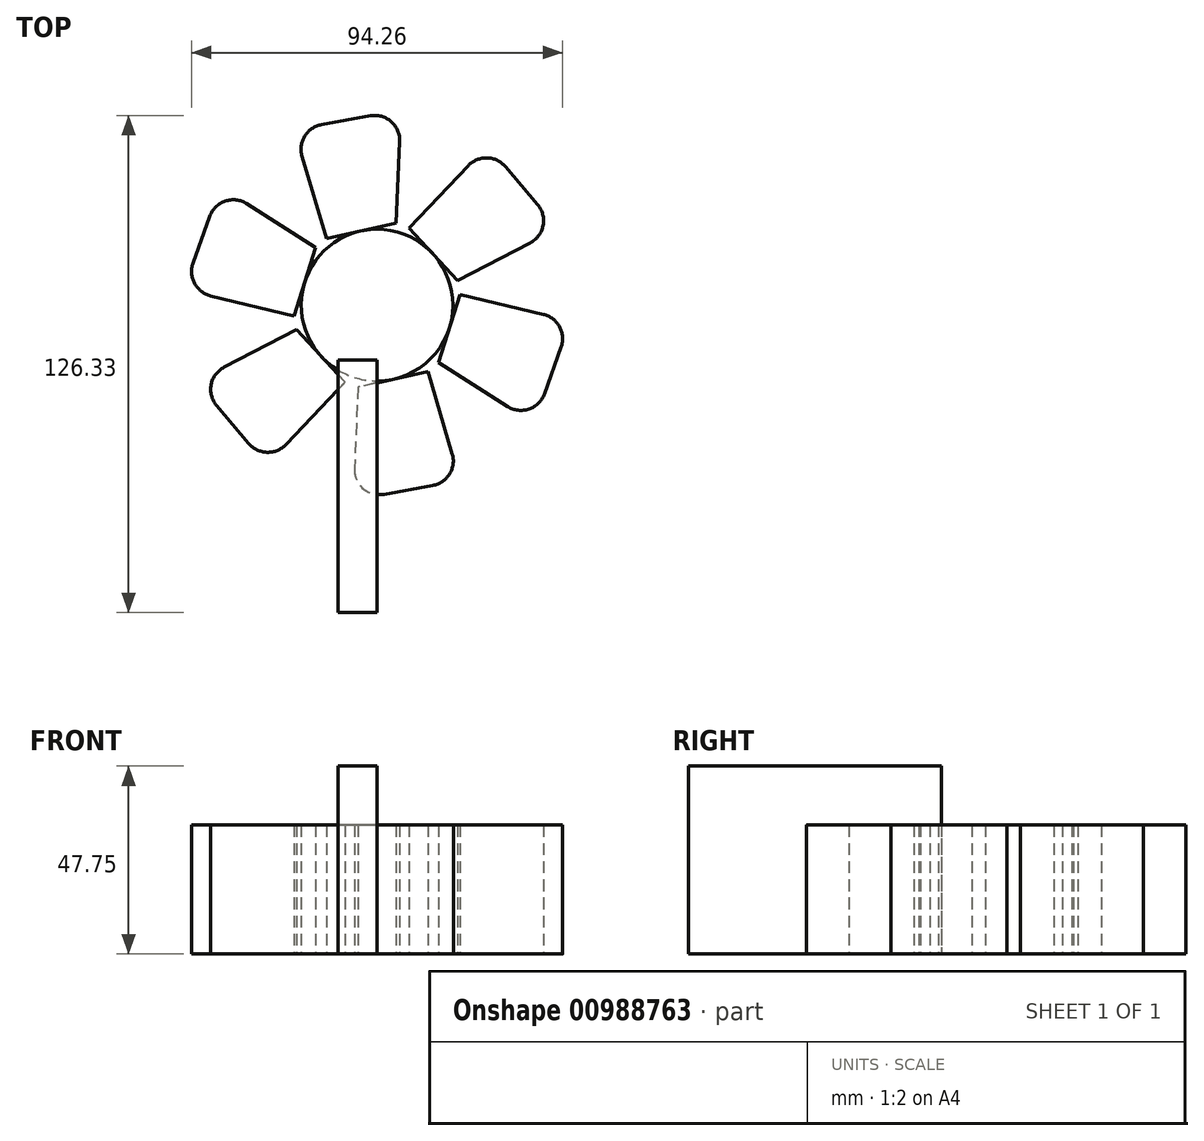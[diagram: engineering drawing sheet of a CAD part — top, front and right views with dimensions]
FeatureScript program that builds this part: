
annotation { "Feature Type Name" : "Feature", "Feature Type Description" : "" }
export const myFeature = defineFeature(function(context is Context, id is Id, definition is map)
    precondition{}
    {
        {
            var Q0;
            Q0=qCreatedBy(makeId("Top.planeOp"),FACE);
            var sketch = newSketch(context, id + "F0", { "sketchPlane" : qUnion([Q0])});
            skCircle(sketch, "E0", {"center": v(0, 0) * mm, "radius": 19.26 * mm});
            skLineSegment(sketch, "E1", {"start": v(8.15, 19.6) * mm, "end": v(20.47, 6.2) * mm});
            skLineSegment(sketch, "E2", {"start": v(20.47, 6.2) * mm, "end": v(38.87, 15.8) * mm});
            skLineSegment(sketch, "E3", {"start": v(40.78, 25.54) * mm, "end": v(32.62, 35.16) * mm});
            skLineSegment(sketch, "E4", {"start": v(23.17, 35.42) * mm, "end": v(8.15, 19.6) * mm});
            skPoint(sketch, "E5.visualSharp", {"position": v(28.04, 40.56) * mm});
            skArc(sketch, "E5.filletArc", {"start": v(32.62, 35.16) * mm, "mid": v(27.95, 37.4) * mm, "end": v(23.17, 35.42) * mm});
            skPoint(sketch, "E6.visualSharp", {"position": v(45.92, 19.47) * mm});
            skArc(sketch, "E6.filletArc", {"start": v(38.87, 15.8) * mm, "mid": v(42.17, 20.2) * mm, "end": v(40.78, 25.54) * mm});
            skArc(sketch, "E7.1.0", {"start": v(-14.14, 45.83) * mm, "mid": v(-18.41, 42.9) * mm, "end": v(-19.1, 37.78) * mm});
            skLineSegment(sketch, "E7.1.1", {"start": v(-1.72, 48.08) * mm, "end": v(-14.14, 45.83) * mm});
            skArc(sketch, "E7.1.2", {"start": v(5.75, 41.56) * mm, "mid": v(3.58, 46.62) * mm, "end": v(-1.72, 48.08) * mm});
            skLineSegment(sketch, "E7.1.3", {"start": v(4.86, 20.83) * mm, "end": v(5.75, 41.56) * mm});
            skLineSegment(sketch, "E7.1.4", {"start": v(-19.1, 37.78) * mm, "end": v(-12.9, 16.85) * mm});
            skLineSegment(sketch, "E7.1.5", {"start": v(-12.9, 16.85) * mm, "end": v(4.86, 20.83) * mm});
            skArc(sketch, "E7.2.0", {"start": v(-46.76, 10.67) * mm, "mid": v(-46.37, 5.5) * mm, "end": v(-42.26, 2.35) * mm});
            skLineSegment(sketch, "E7.2.1", {"start": v(-42.5, 22.55) * mm, "end": v(-46.76, 10.67) * mm});
            skArc(sketch, "E7.2.2", {"start": v(-33.12, 25.76) * mm, "mid": v(-38.58, 26.41) * mm, "end": v(-42.5, 22.55) * mm});
            skLineSegment(sketch, "E7.2.3", {"start": v(-15.6, 14.63) * mm, "end": v(-33.12, 25.76) * mm});
            skLineSegment(sketch, "E7.2.4", {"start": v(-42.26, 2.35) * mm, "end": v(-21.04, -2.74) * mm});
            skLineSegment(sketch, "E7.2.5", {"start": v(-21.04, -2.74) * mm, "end": v(-15.6, 14.63) * mm});
            skArc(sketch, "E7.3.0", {"start": v(-32.62, -35.16) * mm, "mid": v(-27.95, -37.4) * mm, "end": v(-23.17, -35.42) * mm});
            skLineSegment(sketch, "E7.3.1", {"start": v(-40.78, -25.54) * mm, "end": v(-32.62, -35.16) * mm});
            skArc(sketch, "E7.3.2", {"start": v(-38.87, -15.8) * mm, "mid": v(-42.17, -20.2) * mm, "end": v(-40.78, -25.54) * mm});
            skLineSegment(sketch, "E7.3.3", {"start": v(-20.47, -6.2) * mm, "end": v(-38.87, -15.8) * mm});
            skLineSegment(sketch, "E7.3.4", {"start": v(-23.17, -35.42) * mm, "end": v(-8.15, -19.6) * mm});
            skLineSegment(sketch, "E7.3.5", {"start": v(-8.15, -19.6) * mm, "end": v(-20.47, -6.2) * mm});
            skArc(sketch, "E7.4.0", {"start": v(14.14, -45.83) * mm, "mid": v(18.41, -42.9) * mm, "end": v(19.1, -37.78) * mm});
            skLineSegment(sketch, "E7.4.1", {"start": v(1.72, -48.08) * mm, "end": v(14.14, -45.83) * mm});
            skArc(sketch, "E7.4.2", {"start": v(-5.75, -41.56) * mm, "mid": v(-3.58, -46.62) * mm, "end": v(1.72, -48.08) * mm});
            skLineSegment(sketch, "E7.4.3", {"start": v(-4.86, -20.83) * mm, "end": v(-5.75, -41.56) * mm});
            skLineSegment(sketch, "E7.4.4", {"start": v(19.1, -37.78) * mm, "end": v(12.9, -16.85) * mm});
            skLineSegment(sketch, "E7.4.5", {"start": v(12.9, -16.85) * mm, "end": v(-4.86, -20.83) * mm});
            skArc(sketch, "E7.5.0", {"start": v(46.76, -10.67) * mm, "mid": v(46.37, -5.5) * mm, "end": v(42.26, -2.35) * mm});
            skLineSegment(sketch, "E7.5.1", {"start": v(42.5, -22.55) * mm, "end": v(46.76, -10.67) * mm});
            skArc(sketch, "E7.5.2", {"start": v(33.12, -25.76) * mm, "mid": v(38.58, -26.41) * mm, "end": v(42.5, -22.55) * mm});
            skLineSegment(sketch, "E7.5.3", {"start": v(15.6, -14.63) * mm, "end": v(33.12, -25.76) * mm});
            skLineSegment(sketch, "E7.5.4", {"start": v(42.26, -2.35) * mm, "end": v(21.04, 2.74) * mm});
            skLineSegment(sketch, "E7.5.5", {"start": v(21.04, 2.74) * mm, "end": v(15.6, -14.63) * mm});
            skSolve(sketch);
        }
        {
            var Q0;
            Q0=qCreatedBy(makeId("Top.planeOp"),FACE);
            var sketch = newSketch(context, id + "F1", { "sketchPlane" : qUnion([Q0])});
            skLineSegment(sketch, "E8.bottom", {"start": v(0, -13.96) * mm, "end": v(-9.93, -13.96) * mm});
            skLineSegment(sketch, "E8.top", {"start": v(0, -78.14) * mm, "end": v(-9.93, -78.14) * mm});
            skLineSegment(sketch, "E8.left", {"start": v(0, -13.96) * mm, "end": v(0, -78.14) * mm});
            skLineSegment(sketch, "E8.right", {"start": v(-9.93, -13.96) * mm, "end": v(-9.93, -78.14) * mm});
            skSolve(sketch);
        }
        {
            var Q0;
            Q0=makeQuery(id+"F1.imprint","IMPRINT",FACE,{"disambiguationData":[TD([[makeQuery(id+"F1.imprint","IMPRINT",EDGE,{"derivedFrom":sQuery(id+"F1.wireOp",EDGE,"E8.bottom")}),1.0]])]});
            extrude(context, id + "F2", {"entities" : qUnion([Q0]), "depth" : 47.75 * mm, "offsetDistance" : 25.4 * mm});
        }
        {
            var Q0;
            Q0=makeQuery(id+"F0.imprint","IMPRINT",FACE,{"disambiguationData":[TD([[makeQuery(id+"F0.imprint","IMPRINT",EDGE,{"derivedFrom":sQuery(id+"F0.wireOp",EDGE,"E7.2.0")}),1.0]])]});
            var Q1;
            Q1=makeQuery(id+"F0.imprint","IMPRINT",FACE,{"disambiguationData":[TD([[makeQuery(id+"F0.imprint","IMPRINT",EDGE,{"derivedFrom":sQuery(id+"F0.wireOp",EDGE,"E7.1.0")}),1.0]])]});
            var Q2;
            {var subQ0=sQuery(id+"F0.wireOp",EDGE,"E2");Q2=makeQuery(id+"F0.imprint","IMPRINT",FACE,{"disambiguationData":[TD([[makeQuery(id+"F0.imprint","IMPRINT",EDGE,{"derivedFrom":subQ0}),1.0]])]});}
            var Q3;
            Q3=makeQuery(id+"F0.imprint","IMPRINT",FACE,{"disambiguationData":[TD([[makeQuery(id+"F0.imprint","IMPRINT",EDGE,{"derivedFrom":sQuery(id+"F0.wireOp",EDGE,"E7.5.0")}),1.0]])]});
            var Q4;
            Q4=makeQuery(id+"F0.imprint","IMPRINT",FACE,{"disambiguationData":[TD([[makeQuery(id+"F0.imprint","IMPRINT",EDGE,{"derivedFrom":sQuery(id+"F0.wireOp",EDGE,"E7.4.0")}),1.0]])]});
            var Q5;
            Q5=makeQuery(id+"F0.imprint","IMPRINT",FACE,{"disambiguationData":[TD([[makeQuery(id+"F0.imprint","IMPRINT",EDGE,{"derivedFrom":sQuery(id+"F0.wireOp",EDGE,"E7.3.0")}),1.0]])]});
            var Q6;
            {var subQ0=sQuery(id+"F0.wireOp",EDGE,"E0");var subQ4=makeQuery(id+"F0.imprint","INTERSECT",VERTEX,{"derivedFrom":[subQ0,sQuery(id+"F0.wireOp",EDGE,"E7.1.5")]});Q6=makeQuery(id+"F0.imprint","IMPRINT",FACE,{"disambiguationData":[TD([[makeQuery(id+"F0.imprint","IMPRINT",EDGE,{"disambiguationData":[TD([[subQ4,1.0]])],"derivedFrom":subQ0}),1.0]])]});}
            extrude(context, id + "F3", {"entities" : qUnion([Q0, Q1, Q2, Q3, Q4, Q5, Q6]), "depth" : 32.77 * mm, "offsetDistance" : 25.4 * mm});
        }
    });
